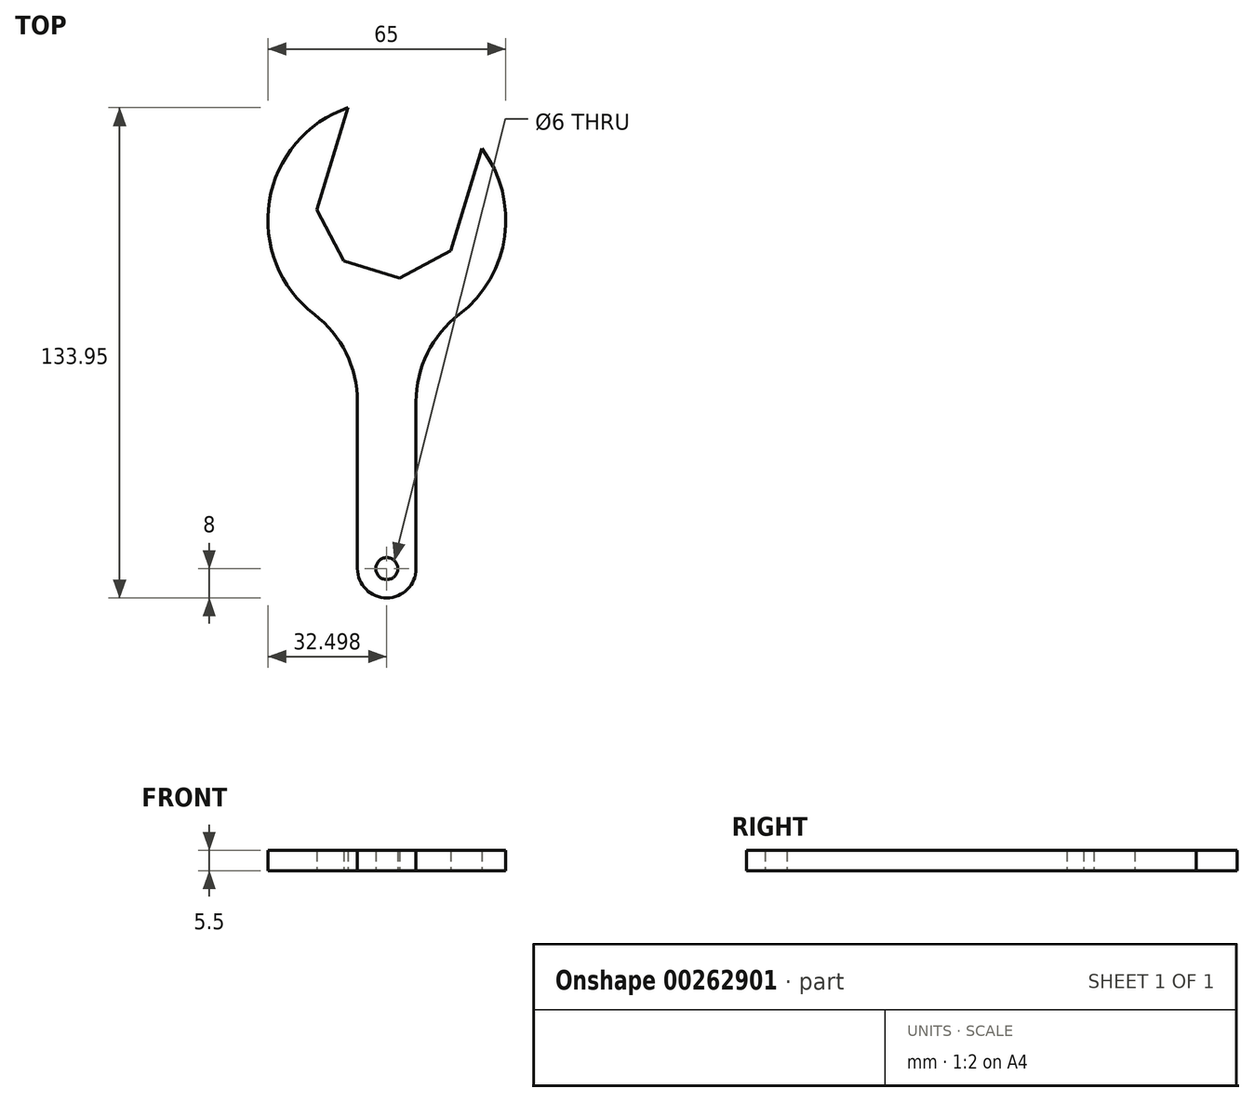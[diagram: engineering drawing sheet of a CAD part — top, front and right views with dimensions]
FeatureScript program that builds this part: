
annotation { "Feature Type Name" : "Feature", "Feature Type Description" : "" }
export const myFeature = defineFeature(function(context is Context, id is Id, definition is map)
    precondition{}
    {
        {
            var Q0;
            Q0=qCreatedBy(makeId("Top.planeOp"),FACE);
            var sketch = newSketch(context, id + "F0", { "sketchPlane" : qUnion([Q0])});
            skArc(sketch, "E0", {"start": v(-9.46, -100) * mm, "mid": v(-1.46, -108) * mm, "end": v(6.54, -100) * mm});
            skLineSegment(sketch, "E1.trimOffspring", {"start": v(6.54, -54.4) * mm, "end": v(6.54, -100) * mm});
            skLineSegment(sketch, "E2.trimOffspring", {"start": v(-9.46, -54.4) * mm, "end": v(-9.46, -100) * mm});
            skCircle(sketch, "E3", {"center": v(-1.46, -100) * mm, "radius": 3 * mm});
            skArc(sketch, "E4", {"start": v(18.3, -30.58) * mm, "mid": v(30.74, -9.18) * mm, "end": v(24.5, 14.78) * mm});
            skArc(sketch, "E5", {"start": v(-9.46, -36.28) * mm, "mid": v(-1.46, -37.28) * mm, "end": v(6.54, -36.28) * mm, "construction": true});
            skLineSegment(sketch, "E6", {"start": v(-1.46, -4.78) * mm, "end": v(-1.46, -100) * mm, "construction": true});
            skLineSegment(sketch, "E7", {"start": v(-14.3, 25.07) * mm, "end": v(-14.3, 25.07) * mm});
            skArc(sketch, "E8", {"start": v(-12.04, 25.95) * mm, "mid": v(-33.54, 0.43) * mm, "end": v(-21.22, -30.58) * mm});
            skPoint(sketch, "E9.visualSharp", {"position": v(6.54, -36.28) * mm});
            skArc(sketch, "E9.filletArc", {"start": v(18.3, -30.58) * mm, "mid": v(9.64, -41.12) * mm, "end": v(6.54, -54.4) * mm});
            skPoint(sketch, "E10.visualSharp", {"position": v(-9.46, -36.28) * mm});
            skArc(sketch, "E10.filletArc", {"start": v(-9.46, -54.4) * mm, "mid": v(-12.56, -41.12) * mm, "end": v(-21.22, -30.58) * mm});
            skCircle(sketch, "E11.cCircle", {"center": v(0, 0) * mm, "radius": 19.1 * mm, "construction": true});
            skLineSegment(sketch, "E11.0", {"start": v(13.15, 15.95) * mm, "end": v(20.58, 1.98) * mm, "construction": true});
            skLineSegment(sketch, "E11.1", {"start": v(24.5, 14.78) * mm, "end": v(15.95, -13.15) * mm});
            skLineSegment(sketch, "E11.2", {"start": v(15.95, -13.15) * mm, "end": v(1.98, -20.58) * mm});
            skLineSegment(sketch, "E11.3", {"start": v(1.98, -20.58) * mm, "end": v(-13.15, -15.95) * mm});
            skLineSegment(sketch, "E11.4", {"start": v(-13.15, -15.95) * mm, "end": v(-20.58, -1.98) * mm});
            skLineSegment(sketch, "E11.5", {"start": v(-20.58, -1.98) * mm, "end": v(-12.04, 25.95) * mm});
            skLineSegment(sketch, "E11.6", {"start": v(-15.95, 13.15) * mm, "end": v(-1.98, 20.58) * mm, "construction": true});
            skLineSegment(sketch, "E11.7", {"start": v(-1.98, 20.58) * mm, "end": v(13.15, 15.95) * mm, "construction": true});
            skPoint(sketch, "E11.0.midPoint", {"position": v(16.86, 8.97) * mm});
            skLineSegment(sketch, "E12", {"start": v(0, 0) * mm, "end": v(-5.58, -18.27) * mm, "construction": true});
            skCircle(sketch, "E13.converted", {"center": v(-1.46, -4.78) * mm, "radius": 32.5 * mm, "construction": true});
            skSolve(sketch);
        }
        {
            var Q0;
            Q0=qSketchRegion(id+"F0",true);
            extrude(context, id + "F1", {"entities" : qUnion([Q0]), "depth" : 5.5 * mm});
        }
    });
